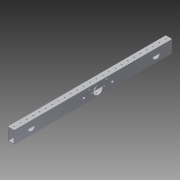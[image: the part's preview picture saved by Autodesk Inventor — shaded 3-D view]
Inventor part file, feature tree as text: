
AUTODESK INVENTOR PART (.ipt)
format: ipt  version: 2014 SP1 (Build 180222100, 222)  size: 454,144 bytes
history: native  units: in
note: dims shown in document units (in); Inventor stores cm internally (conversion verified against a paired STEP export)
features: extrude x9, sketch x8, reference x4, pattern_linear x1
ambient origin geometry x8: Origin, YZ Plane, XZ Plane, XY Plane, X Axis, Y Axis, Z Axis, Center Point
bodies: Solid1 (feature_tree)
feature tree (22):
  extrude  "Extrusion1"  Depth=2.0in
  extrude  "Extrusion2"  Depth=0.1in TaperAngle=0.0deg
  extrude  "Extrusion3"  Depth=1.0in
  extrude  "Extrusion4"  Depth=1.0in TaperAngle=0.0deg
  extrude  "Extrusion5"  Depth=1.125in
  extrude  "Extrusion6"  Depth=0.125in
  extrude  "Extrusion7"  Depth=27.0in TaperAngle=0.0deg
  extrude  "Extrusion8"  Depth=0.2in
  pattern_linear  "Rectangular Pattern1"  Spacing1=0.938in  [1 undecoded]
  extrude  "Extrusion9"  Depth=0.2in
  sketch  "Sketch1"  dims[d0=1.0in d1=2.0in]
  sketch  "Sketch2"  dims[d2=0.1in d3=27.0in d4=0.0in]
  sketch  "Sketch3"  dims[d5=1.0in d6=1.0in]
  sketch  "Sketch5"  dims[d7=1.0in d8=27.0in d9=0.0in]
  reference  "Reference1"
  reference  "Reference2"
  reference  "Reference3"
  reference  "Reference4"
  sketch  "Sketch6"  dims[d11=1.0625in d12=1.125in]
  sketch  "Sketch7"  dims[d14=1.125in d16=0.125in]
  sketch  "Sketch8"  dims[d18=1.5in d19=27.0in d20=0.0in]
  sketch  "Sketch9"  dims[d21=0.938in d22=0.2in d23=0.938in d24=0.2in d25=2.25in d26=2.25in d27=0.4in d28=1.0in d29=0.0in d30=1.0in d31=0.0in d32=0.5in d33=0.003in d34=135.0deg d35=135.0deg d36=0.003in d37=135.0deg d38=135.0deg d39=0.5in d40=0.003in d41=0.003in d42=0.003in d43=0.003in d44=27.0in d45=0.0in d46=135.0deg d47=135.0deg d48=0.5in d50=0.003in d51=0.003in d52=27.0in d53=0.0in d54=0.003in d55=0.5in d56=0.164in d57=27.0in d58=0.0in d59=10.6299in d61=1.0in d62=1.0in d63=1.0in d64=1.0in d65=1.0in d66=1.0in d67=0.0in d68=9.2in d70=10.55in d71=2.5in d72=2.75in d73=0.0625in d74=0.0625in]
note: 1 required parameter value undecoded (feature->parameter linkage not recoverable at this tier; creation-order binding heuristic only, values carry confidence <= 0.55)
